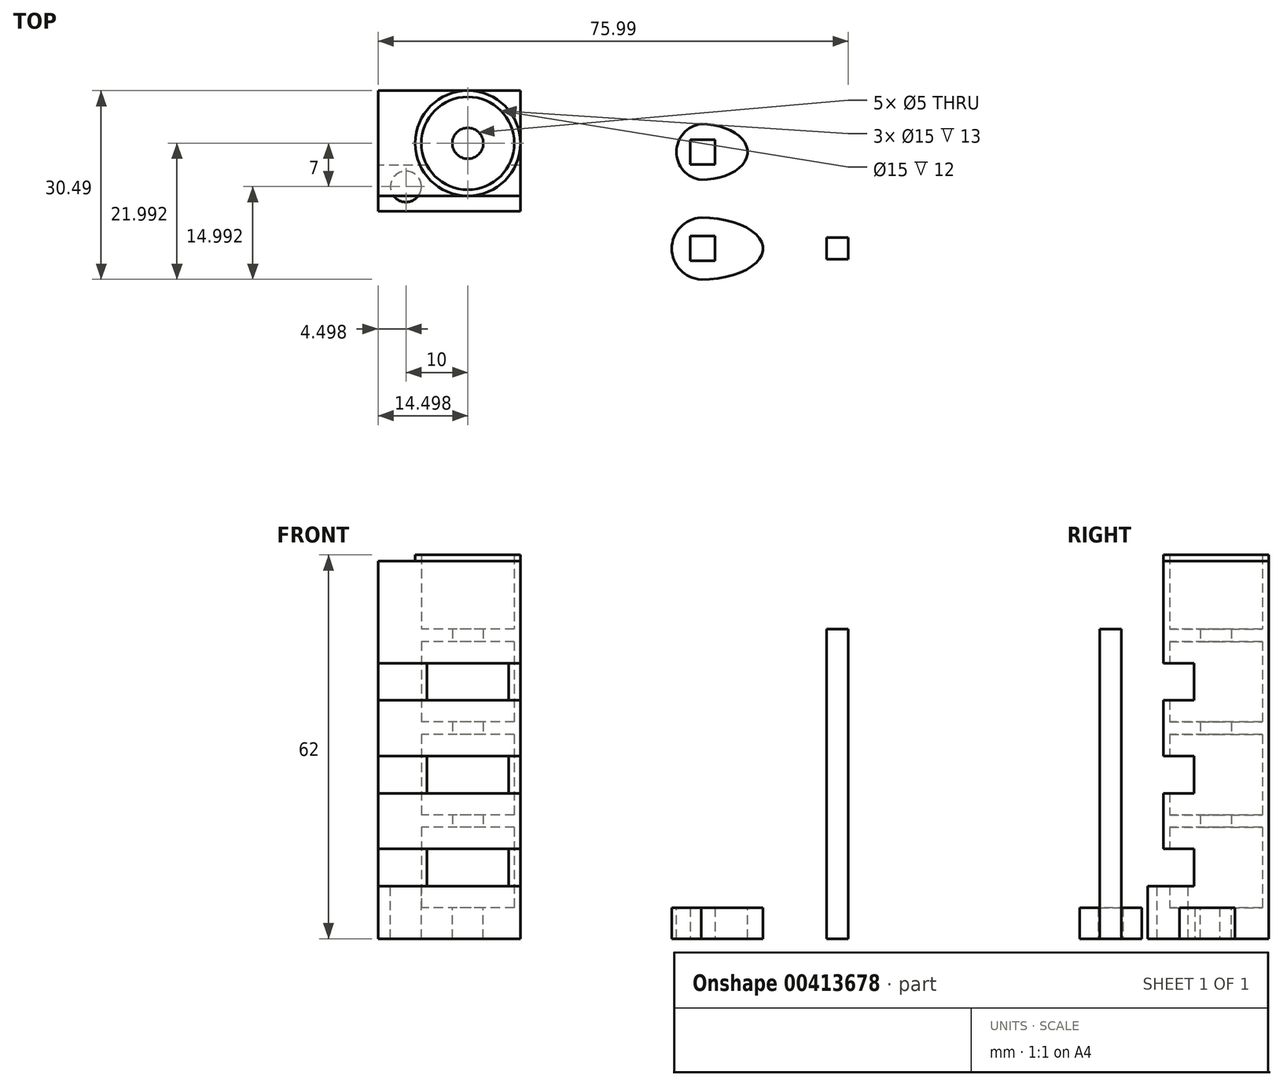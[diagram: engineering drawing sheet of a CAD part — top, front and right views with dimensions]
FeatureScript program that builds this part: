
annotation { "Feature Type Name" : "Feature", "Feature Type Description" : "" }
export const myFeature = defineFeature(function(context is Context, id is Id, definition is map)
    precondition{}
    {
        {
            var Q0;
            Q0=qCreatedBy(makeId("Top.planeOp"),FACE);
            var sketch = newSketch(context, id + "F0", { "sketchPlane" : qUnion([Q0])});
            skEllipticalArc(sketch, "E0", {});
            skArc(sketch, "E1", {"start": v(0, 5) * mm, "mid": v(-4.74, 0) * mm, "end": v(0, -5) * mm});
            skLineSegment(sketch, "E2.bottom", {"start": v(2.26, -2) * mm, "end": v(-1.74, -2) * mm});
            skLineSegment(sketch, "E2.top", {"start": v(2.26, 2) * mm, "end": v(-1.74, 2) * mm});
            skLineSegment(sketch, "E2.left", {"start": v(2.26, -2) * mm, "end": v(2.26, 2) * mm});
            skLineSegment(sketch, "E2.right", {"start": v(-1.74, -2) * mm, "end": v(-1.74, 2) * mm});
            const initialGuessF0  = {"E0": [0, 0, 1, 0, 0.01, 0.004993372962613075, 4.71238898038469, 1.5707963267948966]};
            skSetInitialGuess(sketch, initialGuessF0);
            skSolve(sketch);
        }
        {
            var Q0;
            Q0 = qSketchRegion(id + "F0", true);
            extrude(context, id + "F1", {"entities" : qUnion([Q0]), "depth" : 5 * mm});
        }
        {
            var Q0;
            Q0=qCreatedBy(makeId("Top.planeOp"),FACE);
            var sketch = newSketch(context, id + "F2", { "sketchPlane" : qUnion([Q0])});
            skLineSegment(sketch, "E3.bottom", {"start": v(23.8, 1.75) * mm, "end": v(20.3, 1.75) * mm});
            skLineSegment(sketch, "E3.top", {"start": v(23.8, -1.75) * mm, "end": v(20.3, -1.75) * mm});
            skLineSegment(sketch, "E3.left", {"start": v(23.8, 1.75) * mm, "end": v(23.8, -1.75) * mm});
            skLineSegment(sketch, "E3.right", {"start": v(20.3, 1.75) * mm, "end": v(20.3, -1.75) * mm});
            skPoint(sketch, "E3.middle", {"position": v(22.04, 0) * mm});
            skSolve(sketch);
        }
        {
            var Q0;
            Q0 = qSketchRegion(id + "F2", true);
            extrude(context, id + "F3", {"entities" : qUnion([Q0]), "depth" : 50 * mm});
        }
        {
            var Q0;
            Q0=makeQuery(id+"F1.opExtrude","SWEPT_BODY",BODY,{"disambiguationData":[OSD([sQuery(id+"F0.wireOp",EDGE,"E0"),sQuery(id+"F0.wireOp",EDGE,"E1"),sQuery(id+"F0.wireOp",EDGE,"E2.bottom"),sQuery(id+"F0.wireOp",EDGE,"E2.top"),sQuery(id+"F0.wireOp",EDGE,"E2.left"),sQuery(id+"F0.wireOp",EDGE,"E2.right")])]});
            transform(context, id + "F4", {"entities" : qUnion([Q0]), "transformType" : TransformType.TRANSLATION_3D, "dx" : 0 * mm, "dy" : 15.6 * mm, "dz" : 0 * mm, "makeCopy" : true});
        }
        {
            var Q0;
            Q0=makeQuery(id+"F4.opPattern","COPY",FACE,{"derivedFrom":makeQuery(id+"F1.opExtrude","CAP_FACE",FACE,{"disambiguationData":[OSD([sQuery(id+"F0.wireOp",EDGE,"E0"),sQuery(id+"F0.wireOp",EDGE,"E1"),sQuery(id+"F0.wireOp",EDGE,"E2.bottom"),sQuery(id+"F0.wireOp",EDGE,"E2.top"),sQuery(id+"F0.wireOp",EDGE,"E2.left"),sQuery(id+"F0.wireOp",EDGE,"E2.right")])],"isStart":false}),"instanceName":"1"});
            var sketch = newSketch(context, id + "F5", { "sketchPlane" : qUnion([Q0])});
            skEllipse(sketch, "E4", {"center": v(0, 15.6) * mm, "majorRadius": 10 * mm, "minorRadius": 4.5 * mm, "majorAxis": v(1, 0)});
            skEllipticalArc(sketch, "E5", {});
            skPoint(sketch, "E6", {"position": v(0, 20.6) * mm});
            skPoint(sketch, "E7", {"position": v(0, 11.1) * mm});
            skPoint(sketch, "E8", {"position": v(0, 20.1) * mm});
            skArc(sketch, "E9", {"start": v(0, 20.1) * mm, "mid": v(-4, 15.6) * mm, "end": v(0, 11.1) * mm});
            const initialGuessF5  = {"E5": [0, 0.0156, 1, 0, 0.0075, 0.0045, 4.71238898038469, 1.5707963267948966]};
            skSetInitialGuess(sketch, initialGuessF5);
            skSolve(sketch);
        }
        {
            var Q0;
            Q0=makeQuery(id+"F5.imprint","IMPRINT",FACE,{"disambiguationData":[TD([[makeQuery(id+"F5.imprint","IMPRINT",EDGE,{"derivedFrom":sQuery(id+"F5.wireOp",EDGE,"E5")}),-1.0]])]});
            var Q1;
            {var subQ0=sQuery(id+"F5.wireOp",EDGE,"E5");var subQ1=sQuery(id+"F5.wireOp",EDGE,"E4");var subQ2=makeQuery(id+"F5.imprint","INTERSECT",VERTEX,{"disambiguationData":[OD(0.0)],"derivedFrom":[subQ1,subQ0]});Q1=makeQuery(id+"F5.imprint","IMPRINT",FACE,{"disambiguationData":[TD([[makeQuery(id+"F5.imprint","IMPRINT",EDGE,{"disambiguationData":[TD([[subQ2,-1.0]])],"derivedFrom":subQ1}),-1.0]])]});}
            var Q2;
            {var subQ0=sQuery(id+"F5.wireOp",EDGE,"E5");var subQ1=sQuery(id+"F5.wireOp",EDGE,"E4");var subQ2=makeQuery(id+"F5.imprint","INTERSECT",VERTEX,{"disambiguationData":[OD(1.0)],"derivedFrom":[subQ1,subQ0]});Q2=makeQuery(id+"F5.imprint","IMPRINT",FACE,{"disambiguationData":[TD([[makeQuery(id+"F5.imprint","IMPRINT",EDGE,{"disambiguationData":[TD([[subQ2,1.0]])],"derivedFrom":subQ1}),-1.0]])]});}
            var Q3;
            {var subQ0=sQuery(id+"F5.wireOp",EDGE,"E9");Q3=makeQuery(id+"F5.imprint","IMPRINT",FACE,{"disambiguationData":[TD([[makeQuery(id+"F5.imprint","IMPRINT",EDGE,{"derivedFrom":subQ0}),-1.0]])]});}
            extrude(context, id + "F6", {"entities" : qUnion([Q0, Q1, Q2, Q3]), "operationType" : NewBodyOperationType.REMOVE, "oppositeDirection" : true, "depth" : 25 * mm});
        }
        {
            var Q0;
            Q0=qCreatedBy(makeId("Top.planeOp"),FACE);
            var sketch = newSketch(context, id + "F7", { "sketchPlane" : qUnion([Q0])});
            skCircle(sketch, "E10", {"center": v(-37.7, 17) * mm, "radius": 7.5 * mm});
            skSolve(sketch);
        }
        {
            var Q0;
            Q0=makeQuery(id+"F7.imprint","IMPRINT",FACE,{"disambiguationData":[TD([[makeQuery(id+"F7.imprint","IMPRINT",EDGE,{"derivedFrom":sQuery(id+"F7.wireOp",EDGE,"E10")}),1.0]])]});
            extrude(context, id + "F8", {"entities" : qUnion([Q0]), "depth" : 5 * mm});
        }
        {
            var Q0;
            Q0=makeQuery(id+"F8.opExtrude","CAP_FACE",FACE,{"disambiguationData":[OSD([sQuery(id+"F7.wireOp",EDGE,"E10")])],"isStart":false});
            var sketch = newSketch(context, id + "F9", { "sketchPlane" : qUnion([Q0])});
            skCircle(sketch, "E11", {"center": v(-37.7, 17) * mm, "radius": 2.5 * mm});
            skSolve(sketch);
        }
        {
            var Q0;
            Q0 = qSketchRegion(id + "F9", true);
            extrude(context, id + "F10", {"entities" : qUnion([Q0]), "operationType" : NewBodyOperationType.REMOVE, "endBound" : BoundingType.THROUGH_ALL, "oppositeDirection" : true, "depth" : 25 * mm, "hasSecondDirection" : true, "secondDirectionBound" : SecondDirectionBoundingType.THROUGH_ALL, "secondDirectionOppositeDirection" : false, "secondDirectionDepth" : 25 * mm});
        }
        {
            var Q0;
            Q0=makeQuery(id+"F8.opExtrude","CAP_FACE",FACE,{"disambiguationData":[OSD([sQuery(id+"F7.wireOp",EDGE,"E10")])],"isStart":false});
            var sketch = newSketch(context, id + "F11", { "sketchPlane" : qUnion([Q0])});
            skCircle(sketch, "E12", {"center": v(-37.7, 17) * mm, "radius": 8.5 * mm});
            skSolve(sketch);
        }
        {
            var Q0;
            Q0=makeQuery(id+"F11.imprint","IMPRINT",FACE,{"disambiguationData":[TD([[makeQuery(id+"F11.imprint","IMPRINT",EDGE,{"derivedFrom":sQuery(id+"F11.wireOp",EDGE,"E12")}),1.0]])]});
            extrude(context, id + "F12", {"entities" : qUnion([Q0]), "operationType" : NewBodyOperationType.ADD, "depth" : 7 * mm, "hasSecondDirection" : true, "secondDirectionOppositeDirection" : true, "secondDirectionDepth" : 5 * mm});
        }
        {
            var Q0;
            {var subQ0=sQuery(id+"F7.wireOp",EDGE,"E10");Q0=makeQuery(id+"F12.boolean.opBoolean","MERGE",FACE,{"derivedFrom":[makeQuery(id+"F8.opExtrude","CAP_FACE",FACE,{"disambiguationData":[OSD([subQ0])],"isStart":true}),makeQuery(id+"F12.opExtrude","CAP_FACE",FACE,{"disambiguationData":[OSD([subQ0,sQuery(id+"F11.wireOp",EDGE,"E12")])],"isStart":true})]});}
            var sketch = newSketch(context, id + "F13", { "sketchPlane" : qUnion([Q0])});
            skLineSegment(sketch, "E13.bottom", {"start": v(-29.2, -25.5) * mm, "end": v(-46.2, -25.5) * mm});
            skLineSegment(sketch, "E13.top", {"start": v(-29.2, -8.5) * mm, "end": v(-46.2, -8.5) * mm});
            skLineSegment(sketch, "E13.left", {"start": v(-29.2, -25.5) * mm, "end": v(-29.2, -8.5) * mm});
            skLineSegment(sketch, "E13.right", {"start": v(-46.2, -25.5) * mm, "end": v(-46.2, -8.5) * mm});
            skPoint(sketch, "E13.middle", {"position": v(-37.7, -17) * mm});
            skSolve(sketch);
        }
        {
            var Q0;
            {var subQ0=sQuery(id+"F13.wireOp",EDGE,"E13.left");var subQ1=sQuery(id+"F13.wireOp",EDGE,"E13.bottom");var subQ2=makeQuery(id+"F13.imprint","INTERSECT",VERTEX,{"derivedFrom":[subQ1,subQ0]});Q0=makeQuery(id+"F13.imprint","IMPRINT",FACE,{"disambiguationData":[TD([[makeQuery(id+"F13.imprint","IMPRINT",EDGE,{"disambiguationData":[TD([[subQ2,-1.0]])],"derivedFrom":subQ1}),-1.0]])]});}
            var Q1;
            {var subQ0=sQuery(id+"F13.wireOp",EDGE,"E13.right");var subQ1=sQuery(id+"F13.wireOp",EDGE,"E13.bottom");var subQ2=makeQuery(id+"F13.imprint","INTERSECT",VERTEX,{"derivedFrom":[subQ1,subQ0]});Q1=makeQuery(id+"F13.imprint","IMPRINT",FACE,{"disambiguationData":[TD([[makeQuery(id+"F13.imprint","IMPRINT",EDGE,{"disambiguationData":[TD([[subQ2,1.0]])],"derivedFrom":subQ1}),-1.0]])]});}
            var Q2;
            {var subQ0=sQuery(id+"F13.wireOp",EDGE,"E13.left");var subQ1=sQuery(id+"F13.wireOp",EDGE,"E13.top");var subQ2=makeQuery(id+"F13.imprint","INTERSECT",VERTEX,{"derivedFrom":[subQ1,subQ0]});Q2=makeQuery(id+"F13.imprint","IMPRINT",FACE,{"disambiguationData":[TD([[makeQuery(id+"F13.imprint","IMPRINT",EDGE,{"disambiguationData":[TD([[subQ2,-1.0]])],"derivedFrom":subQ1}),1.0]])]});}
            var Q3;
            {var subQ0=sQuery(id+"F13.wireOp",EDGE,"E13.right");var subQ1=sQuery(id+"F13.wireOp",EDGE,"E13.top");var subQ2=makeQuery(id+"F13.imprint","INTERSECT",VERTEX,{"derivedFrom":[subQ1,subQ0]});Q3=makeQuery(id+"F13.imprint","IMPRINT",FACE,{"disambiguationData":[TD([[makeQuery(id+"F13.imprint","IMPRINT",EDGE,{"disambiguationData":[TD([[subQ2,1.0]])],"derivedFrom":subQ1}),1.0]])]});}
            extrude(context, id + "F14", {"entities" : qUnion([Q0, Q1, Q2, Q3]), "operationType" : NewBodyOperationType.ADD, "oppositeDirection" : true, "depth" : 11 * mm});
        }
        {
            var Q0;
            {var subQ0=sQuery(id+"F13.wireOp",EDGE,"E13.right");Q0=makeQuery(id+"F14.boolean.opBoolean","MERGE",FACE,{"derivedFrom":[makeQuery(id+"F14.opExtrude","SWEPT_FACE",FACE,{"disambiguationData":[OSD([subQ0]),TDD([makeQuery(id+"F13.imprint","IMPRINT",EDGE,{"disambiguationData":[TD([[makeQuery(id+"F13.imprint","INTERSECT",VERTEX,{"derivedFrom":[sQuery(id+"F13.wireOp",EDGE,"E13.bottom"),subQ0]}),-1.0]])],"derivedFrom":subQ0})])]}),makeQuery(id+"F14.opExtrude","SWEPT_FACE",FACE,{"disambiguationData":[OSD([subQ0]),TDD([makeQuery(id+"F13.imprint","IMPRINT",EDGE,{"disambiguationData":[TD([[makeQuery(id+"F13.imprint","INTERSECT",VERTEX,{"derivedFrom":[sQuery(id+"F13.wireOp",EDGE,"E13.top"),subQ0]}),1.0]])],"derivedFrom":subQ0})])]})]});}
            var sketch = newSketch(context, id + "F15", { "sketchPlane" : qUnion([Q0])});
            skLineSegment(sketch, "E14.bottom", {"start": v(-8.5, 7) * mm, "end": v(-13.5, 7) * mm});
            skLineSegment(sketch, "E14.top", {"start": v(-8.5, 12) * mm, "end": v(-13.5, 12) * mm});
            skLineSegment(sketch, "E14.left", {"start": v(-8.5, 7) * mm, "end": v(-8.5, 12) * mm});
            skLineSegment(sketch, "E14.right", {"start": v(-13.5, 7) * mm, "end": v(-13.5, 12) * mm});
            skSolve(sketch);
        }
        {
            var Q0;
            Q0=makeQuery(id+"F12.opExtrude","CAP_FACE",FACE,{"disambiguationData":[OSD([sQuery(id+"F7.wireOp",EDGE,"E10"),sQuery(id+"F11.wireOp",EDGE,"E12")])],"isStart":false});
            extrude(context, id + "F16", {"entities" : qUnion([Q0]), "operationType" : NewBodyOperationType.ADD, "depth" : 50 * mm});
        }
        {
            var Q0;
            Q0=makeQuery(id+"F14.opExtrude","CAP_FACE",FACE,{"disambiguationData":[OSD([sQuery(id+"F11.wireOp",EDGE,"E12"),sQuery(id+"F13.wireOp",EDGE,"E13.bottom"),sQuery(id+"F13.wireOp",EDGE,"E13.right")])],"isStart":false});
            var Q1;
            Q1=makeQuery(id+"F14.opExtrude","CAP_FACE",FACE,{"disambiguationData":[OSD([sQuery(id+"F11.wireOp",EDGE,"E12"),sQuery(id+"F13.wireOp",EDGE,"E13.top"),sQuery(id+"F13.wireOp",EDGE,"E13.right")])],"isStart":false});
            var Q2;
            Q2=makeQuery(id+"F14.opExtrude","CAP_FACE",FACE,{"disambiguationData":[OSD([sQuery(id+"F11.wireOp",EDGE,"E12"),sQuery(id+"F13.wireOp",EDGE,"E13.top"),sQuery(id+"F13.wireOp",EDGE,"E13.left")])],"isStart":false});
            var Q3;
            Q3=makeQuery(id+"F14.opExtrude","CAP_FACE",FACE,{"disambiguationData":[OSD([sQuery(id+"F11.wireOp",EDGE,"E12"),sQuery(id+"F13.wireOp",EDGE,"E13.bottom"),sQuery(id+"F13.wireOp",EDGE,"E13.left")])],"isStart":false});
            extrude(context, id + "F17", {"entities" : qUnion([Q0, Q1, Q2, Q3]), "operationType" : NewBodyOperationType.ADD, "depth" : 50 * mm});
        }
        {
            var Q0;
            {var subQ8=sQuery(id+"F15.wireOp",EDGE,"E14.bottom");Q0=makeQuery(id+"F15.imprint","IMPRINT",FACE,{"disambiguationData":[TD([[makeQuery(id+"F15.imprint","IMPRINT",EDGE,{"derivedFrom":subQ8}),1.0]])]});}
            var sketch = newSketch(context, id + "F18", { "sketchPlane" : qUnion([Q0])});
            skLineSegment(sketch, "E15.bottom", {"start": v(-8.5, 5) * mm, "end": v(-13.45, 5) * mm});
            skLineSegment(sketch, "E15.top", {"start": v(-8.5, 8.5) * mm, "end": v(-13.45, 8.5) * mm});
            skLineSegment(sketch, "E15.left", {"start": v(-8.5, 5) * mm, "end": v(-8.5, 8.5) * mm});
            skLineSegment(sketch, "E15.right", {"start": v(-13.45, 5) * mm, "end": v(-13.45, 8.5) * mm});
            skLineSegment(sketch, "E16.top", {"start": v(-8.5, 14.5) * mm, "end": v(-13.45, 14.5) * mm});
            skLineSegment(sketch, "E16.left", {"start": v(-8.5, 8.5) * mm, "end": v(-8.5, 14.5) * mm});
            skLineSegment(sketch, "E16.right", {"start": v(-13.45, 8.5) * mm, "end": v(-13.45, 14.5) * mm});
            skLineSegment(sketch, "E17.bottom", {"start": v(-13.45, 14.5) * mm, "end": v(-8.5, 14.5) * mm});
            skLineSegment(sketch, "E17.top", {"start": v(-13.45, 18) * mm, "end": v(-8.5, 18) * mm});
            skLineSegment(sketch, "E17.left", {"start": v(-13.45, 14.5) * mm, "end": v(-13.45, 18) * mm});
            skLineSegment(sketch, "E17.right", {"start": v(-8.5, 14.5) * mm, "end": v(-8.5, 18) * mm});
            skLineSegment(sketch, "E18.bottom", {"start": v(-8.5, 18) * mm, "end": v(-25.5, 18) * mm});
            skLineSegment(sketch, "E18.top", {"start": v(-8.5, 20) * mm, "end": v(-25.5, 20) * mm});
            skLineSegment(sketch, "E18.left", {"start": v(-8.5, 18) * mm, "end": v(-8.5, 20) * mm});
            skLineSegment(sketch, "E18.right", {"start": v(-25.5, 18) * mm, "end": v(-25.5, 20) * mm});
            skLineSegment(sketch, "E19.0.1.0", {"start": v(-8.5, 33) * mm, "end": v(-25.5, 33) * mm});
            skLineSegment(sketch, "E19.0.1.1", {"start": v(-13.45, 29.5) * mm, "end": v(-13.45, 33) * mm});
            skLineSegment(sketch, "E19.0.1.2", {"start": v(-8.5, 23.5) * mm, "end": v(-8.5, 29.5) * mm});
            skLineSegment(sketch, "E19.0.1.3", {"start": v(-8.5, 29.5) * mm, "end": v(-8.5, 33) * mm});
            skLineSegment(sketch, "E19.0.1.4", {"start": v(-13.45, 23.5) * mm, "end": v(-13.45, 29.5) * mm});
            skLineSegment(sketch, "E19.0.1.5", {"start": v(-8.5, 35) * mm, "end": v(-25.5, 35) * mm});
            skLineSegment(sketch, "E19.0.1.6", {"start": v(-8.5, 23.5) * mm, "end": v(-13.45, 23.5) * mm});
            skLineSegment(sketch, "E19.0.1.7", {"start": v(-8.5, 20) * mm, "end": v(-13.45, 20) * mm});
            skLineSegment(sketch, "E19.0.1.8", {"start": v(-13.45, 29.5) * mm, "end": v(-8.5, 29.5) * mm});
            skLineSegment(sketch, "E19.0.1.9", {"start": v(-8.5, 29.5) * mm, "end": v(-13.45, 29.5) * mm});
            skLineSegment(sketch, "E19.0.1.10", {"start": v(-8.5, 23.5) * mm, "end": v(-13.45, 23.5) * mm});
            skLineSegment(sketch, "E19.0.1.11", {"start": v(-13.45, 33) * mm, "end": v(-8.5, 33) * mm});
            skLineSegment(sketch, "E19.0.1.12", {"start": v(-8.5, 20) * mm, "end": v(-8.5, 23.5) * mm});
            skLineSegment(sketch, "E19.0.1.13", {"start": v(-25.5, 33) * mm, "end": v(-25.5, 35) * mm});
            skLineSegment(sketch, "E19.0.1.14", {"start": v(-8.5, 33) * mm, "end": v(-8.5, 35) * mm});
            skLineSegment(sketch, "E19.0.1.15", {"start": v(-13.45, 20) * mm, "end": v(-13.45, 23.5) * mm});
            skLineSegment(sketch, "E19.0.2.0", {"start": v(-8.5, 48) * mm, "end": v(-25.5, 48) * mm});
            skLineSegment(sketch, "E19.0.2.1", {"start": v(-13.45, 44.5) * mm, "end": v(-13.45, 48) * mm});
            skLineSegment(sketch, "E19.0.2.2", {"start": v(-8.5, 38.5) * mm, "end": v(-8.5, 44.5) * mm});
            skLineSegment(sketch, "E19.0.2.3", {"start": v(-8.5, 44.5) * mm, "end": v(-8.5, 48) * mm});
            skLineSegment(sketch, "E19.0.2.4", {"start": v(-13.45, 38.5) * mm, "end": v(-13.45, 44.5) * mm});
            skLineSegment(sketch, "E19.0.2.5", {"start": v(-8.5, 50) * mm, "end": v(-25.5, 50) * mm});
            skLineSegment(sketch, "E19.0.2.6", {"start": v(-8.5, 38.5) * mm, "end": v(-13.45, 38.5) * mm});
            skLineSegment(sketch, "E19.0.2.7", {"start": v(-8.5, 35) * mm, "end": v(-13.45, 35) * mm});
            skLineSegment(sketch, "E19.0.2.8", {"start": v(-13.45, 44.5) * mm, "end": v(-8.5, 44.5) * mm});
            skLineSegment(sketch, "E19.0.2.9", {"start": v(-8.5, 44.5) * mm, "end": v(-13.45, 44.5) * mm});
            skLineSegment(sketch, "E19.0.2.10", {"start": v(-8.5, 38.5) * mm, "end": v(-13.45, 38.5) * mm});
            skLineSegment(sketch, "E19.0.2.11", {"start": v(-13.45, 48) * mm, "end": v(-8.5, 48) * mm});
            skLineSegment(sketch, "E19.0.2.12", {"start": v(-8.5, 35) * mm, "end": v(-8.5, 38.5) * mm});
            skLineSegment(sketch, "E19.0.2.13", {"start": v(-25.5, 48) * mm, "end": v(-25.5, 50) * mm});
            skLineSegment(sketch, "E19.0.2.14", {"start": v(-8.5, 48) * mm, "end": v(-8.5, 50) * mm});
            skLineSegment(sketch, "E19.0.2.15", {"start": v(-13.45, 35) * mm, "end": v(-13.45, 38.5) * mm});
            skLineSegment(sketch, "E19.direction1", {"start": v(-13.45, 5) * mm, "end": v(11.55, 5) * mm, "construction": true});
            skLineSegment(sketch, "E19.direction2", {"start": v(-13.45, 5) * mm, "end": v(-13.45, 20) * mm, "construction": true});
            skSolve(sketch);
        }
        {
            var Q0;
            Q0=makeQuery(id+"F18.imprint","IMPRINT",FACE,{"disambiguationData":[TD([[makeQuery(id+"F18.imprint","IMPRINT",EDGE,{"derivedFrom":sQuery(id+"F18.wireOp",EDGE,"E18.top")}),1.0]])]});
            var Q1;
            Q1=makeQuery(id+"F18.imprint","IMPRINT",FACE,{"disambiguationData":[TD([[makeQuery(id+"F18.imprint","IMPRINT",EDGE,{"derivedFrom":sQuery(id+"F18.wireOp",EDGE,"E19.0.2.0")}),-1.0]])]});
            var Q2;
            Q2=makeQuery(id+"F18.imprint","IMPRINT",FACE,{"disambiguationData":[TD([[makeQuery(id+"F18.imprint","IMPRINT",EDGE,{"derivedFrom":sQuery(id+"F18.wireOp",EDGE,"E19.0.1.0")}),-1.0]])]});
            extrude(context, id + "F19", {"entities" : qUnion([Q0, Q1, Q2]), "operationType" : NewBodyOperationType.ADD, "oppositeDirection" : true, "depth" : 17 * mm});
        }
        {
            var Q0;
            Q0=makeQuery(id+"F18.imprint","IMPRINT",FACE,{"disambiguationData":[TD([[makeQuery(id+"F18.imprint","IMPRINT",EDGE,{"derivedFrom":sQuery(id+"F18.wireOp",EDGE,"E19.0.2.2")}),1.0]])]});
            var Q1;
            Q1=makeQuery(id+"F18.imprint","IMPRINT",FACE,{"disambiguationData":[TD([[makeQuery(id+"F18.imprint","IMPRINT",EDGE,{"derivedFrom":sQuery(id+"F18.wireOp",EDGE,"E19.0.1.2")}),1.0]])]});
            var Q2;
            Q2=makeQuery(id+"F18.imprint","IMPRINT",FACE,{"disambiguationData":[TD([[makeQuery(id+"F18.imprint","IMPRINT",EDGE,{"derivedFrom":sQuery(id+"F18.wireOp",EDGE,"E15.top")}),-1.0]])]});
            extrude(context, id + "F20", {"entities" : qUnion([Q0, Q1, Q2]), "operationType" : NewBodyOperationType.REMOVE, "oppositeDirection" : true, "depth" : 25 * mm});
        }
        {
            var Q0;
            {var subQ0=sQuery(id+"F13.wireOp",EDGE,"E13.right");var subQ1=sQuery(id+"F13.wireOp",EDGE,"E13.top");var subQ2=sQuery(id+"F11.wireOp",EDGE,"E12");var subQ3=sQuery(id+"F13.wireOp",EDGE,"E13.left");var subQ4=sQuery(id+"F13.wireOp",EDGE,"E13.bottom");var subQ5=sQuery(id+"F7.wireOp",EDGE,"E10");Q0=makeQuery(id+"F14.boolean.opBoolean","MERGE",FACE,{"derivedFrom":[makeQuery(id+"F12.boolean.opBoolean","MERGE",FACE,{"derivedFrom":[makeQuery(id+"F8.opExtrude","CAP_FACE",FACE,{"disambiguationData":[OSD([subQ5])],"isStart":true}),makeQuery(id+"F12.opExtrude","CAP_FACE",FACE,{"disambiguationData":[OSD([subQ5,subQ2])],"isStart":true})]}),makeQuery(id+"F14.opExtrude","CAP_FACE",FACE,{"disambiguationData":[OSD([subQ2,subQ4,subQ3])],"isStart":true}),makeQuery(id+"F14.opExtrude","CAP_FACE",FACE,{"disambiguationData":[OSD([subQ2,subQ4,subQ0])],"isStart":true}),makeQuery(id+"F14.opExtrude","CAP_FACE",FACE,{"disambiguationData":[OSD([subQ2,subQ1,subQ3])],"isStart":true}),makeQuery(id+"F14.opExtrude","CAP_FACE",FACE,{"disambiguationData":[OSD([subQ2,subQ1,subQ0])],"isStart":true})]});}
            var sketch = newSketch(context, id + "F21", { "sketchPlane" : qUnion([Q0])});
            skCircle(sketch, "E20", {"center": v(-37.7, -17) * mm, "radius": 2.5 * mm});
            skSolve(sketch);
        }
        {
            var Q0;
            Q0 = qSketchRegion(id + "F21", true);
            extrude(context, id + "F22", {"entities" : qUnion([Q0]), "operationType" : NewBodyOperationType.REMOVE, "endBound" : BoundingType.THROUGH_ALL, "oppositeDirection" : true, "depth" : 25 * mm});
        }
        {
            var Q0;
            Q0=makeQuery(id+"F8.opExtrude","SWEPT_BODY",BODY,{"disambiguationData":[OSD([sQuery(id+"F7.wireOp",EDGE,"E10")])]});
            transform(context, id + "F23", {"entities" : qUnion([Q0]), "transformType" : TransformType.TRANSLATION_3D, "dx" : 0 * mm, "dy" : 0 * mm, "dz" : -75 * mm, "makeCopy" : true});
        }
        {
            var Q0;
            {var subQ0=sQuery(id+"F13.wireOp",EDGE,"E13.right");var subQ1=sQuery(id+"F13.wireOp",EDGE,"E13.top");var subQ2=makeQuery(id+"F13.imprint","INTERSECT",VERTEX,{"derivedFrom":[subQ1,subQ0]});var subQ3=sQuery(id+"F11.wireOp",EDGE,"E12");var subQ9=sQuery(id+"F13.wireOp",EDGE,"E13.left");var subQ10=makeQuery(id+"F13.imprint","INTERSECT",VERTEX,{"derivedFrom":[subQ1,subQ9]});var subQ15=makeQuery(id+"F13.imprint","IMPRINT",EDGE,{"disambiguationData":[TD([[subQ2,1.0]])],"derivedFrom":subQ1});var subQ16=makeQuery(id+"F13.imprint","IMPRINT",EDGE,{"disambiguationData":[TD([[subQ10,-1.0]])],"derivedFrom":subQ1});Q0=makeQuery(id+"F23.opPattern","COPY",FACE,{"derivedFrom":makeQuery(id+"F20.boolean.opBoolean","SPLIT",FACE,{"disambiguationData":[TD([makeQuery(id+"F12.opExtrude","SWEPT_FACE",FACE,{"disambiguationData":[OSD([subQ3])]})])],"derivedFrom":makeQuery(id+"F17.boolean.opBoolean","MERGE",FACE,{"derivedFrom":[makeQuery(id+"F14.boolean.opBoolean","MERGE",FACE,{"derivedFrom":[makeQuery(id+"F14.opExtrude","SWEPT_FACE",FACE,{"disambiguationData":[OSD([subQ1]),TDD([subQ16])]}),makeQuery(id+"F14.opExtrude","SWEPT_FACE",FACE,{"disambiguationData":[OSD([subQ1]),TDD([subQ15])]})]}),makeQuery(id+"F17.opExtrude","SWEPT_FACE",FACE,{"disambiguationData":[OSD([subQ1]),TDD([makeQuery(id+"F14.opExtrude","CAP_EDGE",EDGE,{"disambiguationData":[OSD([subQ1]),TDD([subQ16])],"isStart":false})])]}),makeQuery(id+"F17.opExtrude","SWEPT_FACE",FACE,{"disambiguationData":[OSD([subQ1]),TDD([makeQuery(id+"F14.opExtrude","CAP_EDGE",EDGE,{"disambiguationData":[OSD([subQ1]),TDD([subQ15])],"isStart":false})])]})]})}),"instanceName":"1"});}
            var sketch = newSketch(context, id + "F24", { "sketchPlane" : qUnion([Q0])});
            skLineSegment(sketch, "E21.bottom", {"start": v(-60.82, -8.34) * mm, "end": v(-19.88, -8.34) * mm});
            skLineSegment(sketch, "E21.top", {"start": v(-60.82, -38.03) * mm, "end": v(-19.88, -38.03) * mm});
            skLineSegment(sketch, "E21.left", {"start": v(-60.82, -8.34) * mm, "end": v(-60.82, -38.03) * mm});
            skLineSegment(sketch, "E21.right", {"start": v(-19.88, -8.34) * mm, "end": v(-19.88, -38.03) * mm});
            skLineSegment(sketch, "E22.bottom", {"start": v(-56.32, -57.37) * mm, "end": v(-19.88, -57.37) * mm});
            skLineSegment(sketch, "E22.top", {"start": v(-56.32, -79.42) * mm, "end": v(-19.88, -79.42) * mm});
            skLineSegment(sketch, "E22.left", {"start": v(-56.32, -57.37) * mm, "end": v(-56.32, -79.42) * mm});
            skLineSegment(sketch, "E22.right", {"start": v(-19.88, -57.37) * mm, "end": v(-19.88, -79.42) * mm});
            skSolve(sketch);
        }
        {
            var Q0;
            Q0 = qSketchRegion(id + "F24", true);
            extrude(context, id + "F25", {"entities" : qUnion([Q0]), "operationType" : NewBodyOperationType.REMOVE, "oppositeDirection" : true, "depth" : 25 * mm});
        }
        {
            var Q0;
            {var subQ0=sQuery(id+"F13.wireOp",EDGE,"E13.right");var subQ2=makeQuery(id+"F13.imprint","IMPRINT",EDGE,{"disambiguationData":[TD([[makeQuery(id+"F13.imprint","INTERSECT",VERTEX,{"derivedFrom":[sQuery(id+"F13.wireOp",EDGE,"E13.top"),subQ0]}),1.0]])],"derivedFrom":subQ0});var subQ3=makeQuery(id+"F13.imprint","IMPRINT",EDGE,{"disambiguationData":[TD([[makeQuery(id+"F13.imprint","INTERSECT",VERTEX,{"derivedFrom":[sQuery(id+"F13.wireOp",EDGE,"E13.bottom"),subQ0]}),-1.0]])],"derivedFrom":subQ0});Q0=makeQuery(id+"F23.opPattern","COPY",FACE,{"derivedFrom":makeQuery(id+"F17.boolean.opBoolean","MERGE",FACE,{"derivedFrom":[makeQuery(id+"F14.boolean.opBoolean","MERGE",FACE,{"derivedFrom":[makeQuery(id+"F14.opExtrude","SWEPT_FACE",FACE,{"disambiguationData":[OSD([subQ0]),TDD([subQ3])]}),makeQuery(id+"F14.opExtrude","SWEPT_FACE",FACE,{"disambiguationData":[OSD([subQ0]),TDD([subQ2])]})]}),makeQuery(id+"F17.opExtrude","SWEPT_FACE",FACE,{"disambiguationData":[OSD([subQ0]),TDD([makeQuery(id+"F14.opExtrude","CAP_EDGE",EDGE,{"disambiguationData":[OSD([subQ0]),TDD([subQ3])],"isStart":false})])]}),makeQuery(id+"F17.opExtrude","SWEPT_FACE",FACE,{"disambiguationData":[OSD([subQ0]),TDD([makeQuery(id+"F14.opExtrude","CAP_EDGE",EDGE,{"disambiguationData":[OSD([subQ0]),TDD([subQ2])],"isStart":false})])]})]}),"instanceName":"1"});}
            extrude(context, id + "F26", {"entities" : qUnion([Q0]), "operationType" : NewBodyOperationType.ADD, "depth" : 5 * mm});
        }
        {
            var Q0;
            Q0=makeQuery(id+"F23.opPattern","COPY",BODY,{"derivedFrom":makeQuery(id+"F8.opExtrude","SWEPT_BODY",BODY,{"disambiguationData":[OSD([sQuery(id+"F7.wireOp",EDGE,"E10")])]}),"instanceName":"1"});
            deleteBodies(context, id + "F27", {"entities" : qUnion([Q0])});
        }
        {
            var Q0;
            {var subQ0=sQuery(id+"F13.wireOp",EDGE,"E13.right");var subQ2=makeQuery(id+"F13.imprint","IMPRINT",EDGE,{"disambiguationData":[TD([[makeQuery(id+"F13.imprint","INTERSECT",VERTEX,{"derivedFrom":[sQuery(id+"F13.wireOp",EDGE,"E13.top"),subQ0]}),1.0]])],"derivedFrom":subQ0});var subQ3=makeQuery(id+"F13.imprint","IMPRINT",EDGE,{"disambiguationData":[TD([[makeQuery(id+"F13.imprint","INTERSECT",VERTEX,{"derivedFrom":[sQuery(id+"F13.wireOp",EDGE,"E13.bottom"),subQ0]}),-1.0]])],"derivedFrom":subQ0});Q0=makeQuery(id+"F17.boolean.opBoolean","MERGE",FACE,{"derivedFrom":[makeQuery(id+"F14.boolean.opBoolean","MERGE",FACE,{"derivedFrom":[makeQuery(id+"F14.opExtrude","SWEPT_FACE",FACE,{"disambiguationData":[OSD([subQ0]),TDD([subQ3])]}),makeQuery(id+"F14.opExtrude","SWEPT_FACE",FACE,{"disambiguationData":[OSD([subQ0]),TDD([subQ2])]})]}),makeQuery(id+"F17.opExtrude","SWEPT_FACE",FACE,{"disambiguationData":[OSD([subQ0]),TDD([makeQuery(id+"F14.opExtrude","CAP_EDGE",EDGE,{"disambiguationData":[OSD([subQ0]),TDD([subQ3])],"isStart":false})])]}),makeQuery(id+"F17.opExtrude","SWEPT_FACE",FACE,{"disambiguationData":[OSD([subQ0]),TDD([makeQuery(id+"F14.opExtrude","CAP_EDGE",EDGE,{"disambiguationData":[OSD([subQ0]),TDD([subQ2])],"isStart":false})])]})]});}
            extrude(context, id + "F28", {"entities" : qUnion([Q0]), "operationType" : NewBodyOperationType.ADD, "depth" : 6 * mm});
        }
        {
            var Q0;
            {var subQ0=sQuery(id+"F18.wireOp",EDGE,"E15.top");Q0=makeQuery(id+"F28.boolean.opBoolean","MERGE",FACE,{"derivedFrom":[makeQuery(id+"F20.boolean.opBoolean","COPY",FACE,{"derivedFrom":makeQuery(id+"F20.opExtrude","SWEPT_FACE",FACE,{"disambiguationData":[OSD([subQ0])]})}),makeQuery(id+"F28.opExtrude","SWEPT_FACE",FACE,{"disambiguationData":[OSD([subQ0])]})]});}
            var sketch = newSketch(context, id + "F29", { "sketchPlane" : qUnion([Q0])});
            skCircle(sketch, "E23", {"center": v(-47.7, 10) * mm, "radius": 2.5 * mm});
            skSolve(sketch);
        }
        {
            var Q0;
            {var subQ0=sQuery(id+"F13.wireOp",EDGE,"E13.right");var subQ8=sQuery(id+"F13.wireOp",EDGE,"E13.top");var subQ10=sQuery(id+"F13.wireOp",EDGE,"E13.left");var subQ11=makeQuery(id+"F13.imprint","INTERSECT",VERTEX,{"derivedFrom":[subQ8,subQ10]});var subQ13=makeQuery(id+"F13.imprint","IMPRINT",EDGE,{"disambiguationData":[TD([[subQ11,-1.0]])],"derivedFrom":subQ8});var subQ14=makeQuery(id+"F17.opExtrude","SWEPT_FACE",FACE,{"disambiguationData":[OSD([subQ8]),TDD([makeQuery(id+"F14.opExtrude","CAP_EDGE",EDGE,{"disambiguationData":[OSD([subQ8]),TDD([subQ13])],"isStart":false})])]});var subQ15=makeQuery(id+"F13.imprint","INTERSECT",VERTEX,{"derivedFrom":[subQ8,subQ0]});var subQ16=makeQuery(id+"F13.imprint","IMPRINT",EDGE,{"disambiguationData":[TD([[subQ15,1.0]])],"derivedFrom":subQ8});var subQ17=makeQuery(id+"F14.opExtrude","SWEPT_FACE",FACE,{"disambiguationData":[OSD([subQ8]),TDD([subQ16])]});var subQ18=makeQuery(id+"F14.opExtrude","SWEPT_FACE",FACE,{"disambiguationData":[OSD([subQ8]),TDD([subQ13])]});var subQ20=sQuery(id+"F7.wireOp",EDGE,"E10");var subQ22=makeQuery(id+"F17.opExtrude","SWEPT_FACE",FACE,{"disambiguationData":[OSD([subQ8]),TDD([makeQuery(id+"F14.opExtrude","CAP_EDGE",EDGE,{"disambiguationData":[OSD([subQ8]),TDD([subQ16])],"isStart":false})])]});var subQ23=makeQuery(id+"F8.opExtrude","CAP_FACE",FACE,{"disambiguationData":[OSD([subQ20])],"isStart":true});Q0=makeQuery(id+"F28.boolean.opBoolean","MERGE",FACE,{"derivedFrom":[makeQuery(id+"F20.boolean.opBoolean","SPLIT",FACE,{"disambiguationData":[TD([subQ23])],"derivedFrom":makeQuery(id+"F17.boolean.opBoolean","MERGE",FACE,{"derivedFrom":[makeQuery(id+"F14.boolean.opBoolean","MERGE",FACE,{"derivedFrom":[subQ18,subQ17]}),subQ14,subQ22]})}),makeQuery(id+"F28.opExtrude","SWEPT_FACE",FACE,{"disambiguationData":[OSD([subQ8,subQ0]),TDD([makeQuery(id+"F20.boolean.opBoolean","SPLIT",EDGE,{"disambiguationData":[TD([subQ23])],"derivedFrom":makeQuery(id+"F17.boolean.opBoolean","MERGE",EDGE,{"derivedFrom":[makeQuery(id+"F14.opExtrude","SWEPT_EDGE",EDGE,{"disambiguationData":[OSD([subQ8,subQ0])]}),makeQuery(id+"F17.opExtrude","SWEPT_EDGE",EDGE,{"disambiguationData":[OSD([subQ8,subQ0])]})]})})])]})]});}
            extrude(context, id + "F30", {"entities" : qUnion([Q0]), "operationType" : NewBodyOperationType.ADD, "depth" : 2.5 * mm});
        }
        {
            var Q0;
            {var subQ0=sQuery(id+"F29.wireOp",EDGE,"E23");var subQ1=sQuery(id+"F18.wireOp",EDGE,"E16.left");var subQ2=sQuery(id+"F18.wireOp",EDGE,"E15.top");var subQ3=sQuery(id+"F18.wireOp",EDGE,"E15.left");var subQ4=makeQuery(id+"F28.boolean.opBoolean","MERGE",EDGE,{"derivedFrom":[makeQuery(id+"F20.boolean.opBoolean","COPY",EDGE,{"derivedFrom":makeQuery(id+"F20.opExtrude","SWEPT_EDGE",EDGE,{"disambiguationData":[OSD([subQ3,subQ2,subQ1])]})}),makeQuery(id+"F28.opExtrude","SWEPT_EDGE",EDGE,{"disambiguationData":[OSD([subQ3,subQ2,subQ1])]})]});var subQ5=makeQuery(id+"F29.imprint","INTERSECT",VERTEX,{"disambiguationData":[OD(0.0)],"derivedFrom":[subQ4,subQ0]});Q0=makeQuery(id+"F29.imprint","IMPRINT",FACE,{"disambiguationData":[TD([[makeQuery(id+"F29.imprint","IMPRINT",EDGE,{"disambiguationData":[TD([[subQ5,1.0]])],"derivedFrom":subQ0}),1.0]])]});}
            var Q1;
            {var subQ0=sQuery(id+"F29.wireOp",EDGE,"E23");var subQ1=sQuery(id+"F18.wireOp",EDGE,"E16.left");var subQ2=sQuery(id+"F18.wireOp",EDGE,"E15.top");var subQ3=sQuery(id+"F18.wireOp",EDGE,"E15.left");var subQ4=makeQuery(id+"F28.boolean.opBoolean","MERGE",EDGE,{"derivedFrom":[makeQuery(id+"F20.boolean.opBoolean","COPY",EDGE,{"derivedFrom":makeQuery(id+"F20.opExtrude","SWEPT_EDGE",EDGE,{"disambiguationData":[OSD([subQ3,subQ2,subQ1])]})}),makeQuery(id+"F28.opExtrude","SWEPT_EDGE",EDGE,{"disambiguationData":[OSD([subQ3,subQ2,subQ1])]})]});var subQ5=makeQuery(id+"F29.imprint","INTERSECT",VERTEX,{"disambiguationData":[OD(0.0)],"derivedFrom":[subQ4,subQ0]});Q1=makeQuery(id+"F29.imprint","IMPRINT",FACE,{"disambiguationData":[TD([[makeQuery(id+"F29.imprint","IMPRINT",EDGE,{"disambiguationData":[TD([[subQ5,-1.0]])],"derivedFrom":subQ0}),1.0]])]});}
            var Q2;
            Q2=sQuery(id+"F29.wireOp",EDGE,"E23");
            extrude(context, id + "F31", {"entities" : qUnion([Q0, Q1]), "operationType" : NewBodyOperationType.REMOVE, "surfaceEntities" : qUnion([Q2]), "endBound" : BoundingType.THROUGH_ALL, "oppositeDirection" : true, "depth" : 25 * mm});
        }
    });
